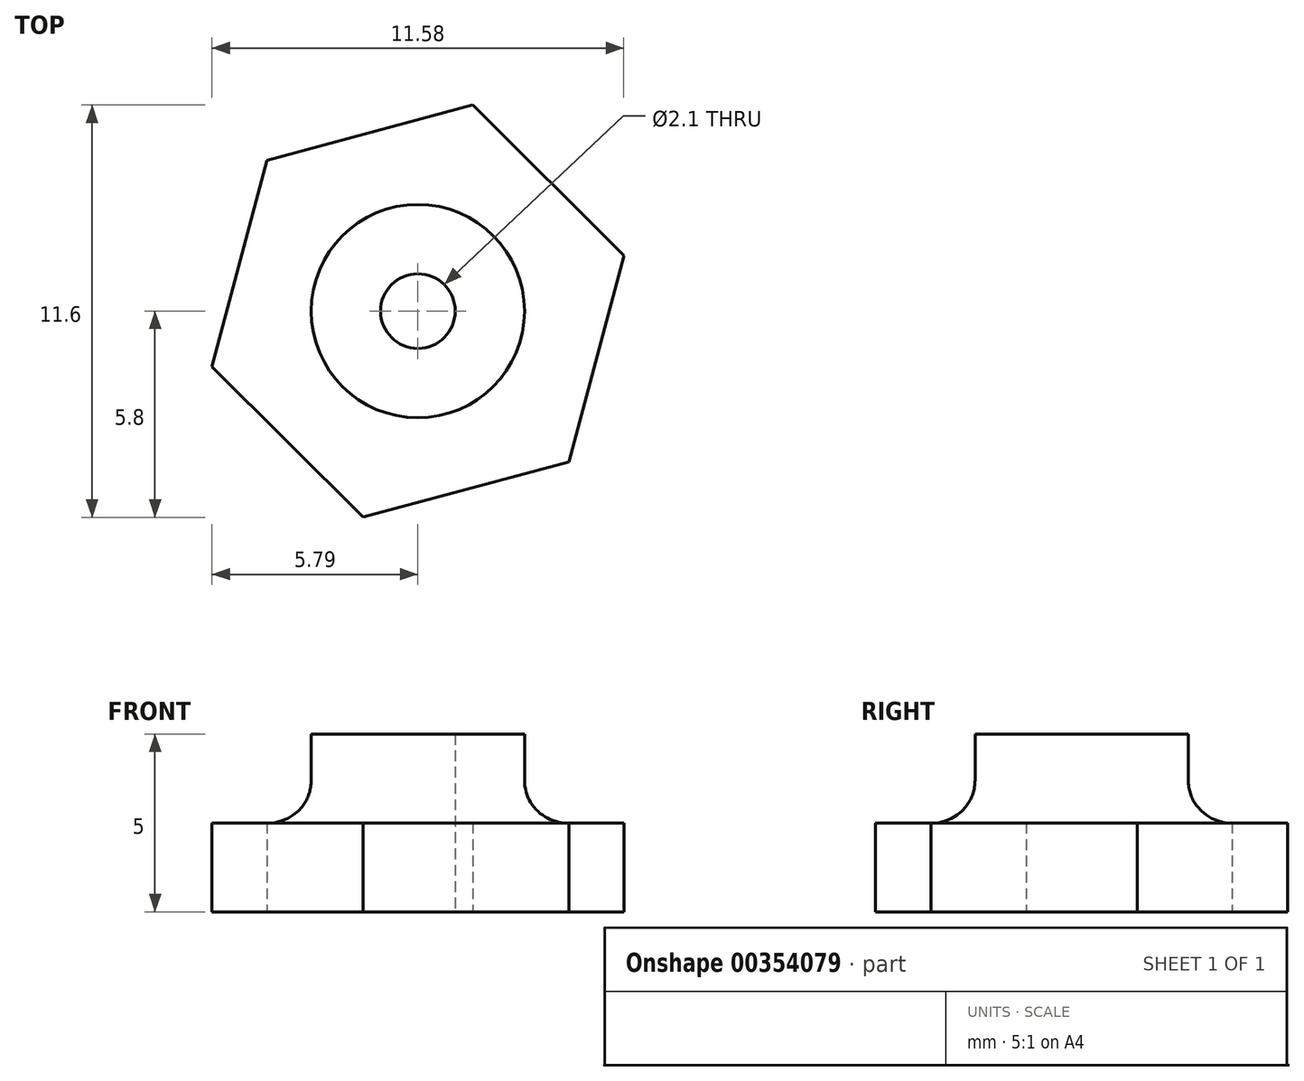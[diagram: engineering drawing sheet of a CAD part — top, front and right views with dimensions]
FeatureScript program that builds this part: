
annotation { "Feature Type Name" : "Feature", "Feature Type Description" : "" }
export const myFeature = defineFeature(function(context is Context, id is Id, definition is map)
    precondition{}
    {
        {
            var Q0;
            Q0=qCreatedBy(makeId("Top.planeOp"),FACE);
            var sketch = newSketch(context, id + "F0", { "sketchPlane" : qUnion([Q0])});
            skCircle(sketch, "E0", {"center": v(0, 0) * mm, "radius": 3 * mm});
            skCircle(sketch, "E1", {"center": v(0, 0) * mm, "radius": 1.05 * mm});
            skCircle(sketch, "E2.cCircle", {"center": v(0, 0) * mm, "radius": 6 * mm, "construction": true});
            skLineSegment(sketch, "E2.0", {"start": v(-4.25, 4.24) * mm, "end": v(1.55, 5.8) * mm});
            skLineSegment(sketch, "E2.1", {"start": v(1.55, 5.8) * mm, "end": v(5.8, 1.56) * mm});
            skLineSegment(sketch, "E2.2", {"start": v(5.8, 1.56) * mm, "end": v(4.25, -4.24) * mm});
            skLineSegment(sketch, "E2.3", {"start": v(4.25, -4.24) * mm, "end": v(-1.55, -5.8) * mm});
            skLineSegment(sketch, "E2.4", {"start": v(-1.55, -5.8) * mm, "end": v(-5.8, -1.56) * mm});
            skLineSegment(sketch, "E2.5", {"start": v(-5.8, -1.56) * mm, "end": v(-4.25, 4.24) * mm});
            skSolve(sketch);
        }
        {
            var Q0;
            Q0=makeQuery(id+"F0.imprint","IMPRINT",FACE,{"disambiguationData":[TD([[makeQuery(id+"F0.imprint","IMPRINT",EDGE,{"derivedFrom":sQuery(id+"F0.wireOp",EDGE,"E0")}),-1.0]])]});
            var Q1;
            Q1=makeQuery(id+"F0.imprint","IMPRINT",FACE,{"disambiguationData":[TD([[makeQuery(id+"F0.imprint","IMPRINT",EDGE,{"derivedFrom":sQuery(id+"F0.wireOp",EDGE,"E0")}),1.0]])]});
            extrude(context, id + "F1", {"entities" : qUnion([Q0, Q1]), "depth" : 2.5 * mm});
        }
        {
            var Q0;
            Q0=makeQuery(id+"F0.imprint","IMPRINT",FACE,{"disambiguationData":[TD([[makeQuery(id+"F0.imprint","IMPRINT",EDGE,{"derivedFrom":sQuery(id+"F0.wireOp",EDGE,"E0")}),1.0]])]});
            extrude(context, id + "F2", {"entities" : qUnion([Q0]), "operationType" : NewBodyOperationType.ADD, "depth" : 5 * mm});
        }
        {
            var Q0;
            Q0=makeQuery(id+"F2.boolean.opBoolean","INTERSECT",EDGE,{"derivedFrom":[makeQuery(id+"F1.opExtrude","CAP_FACE",FACE,{"disambiguationData":[OSD([sQuery(id+"F0.wireOp",EDGE,"E1"),sQuery(id+"F0.wireOp",EDGE,"E2.0"),sQuery(id+"F0.wireOp",EDGE,"E2.1"),sQuery(id+"F0.wireOp",EDGE,"E2.2"),sQuery(id+"F0.wireOp",EDGE,"E2.3"),sQuery(id+"F0.wireOp",EDGE,"E2.4"),sQuery(id+"F0.wireOp",EDGE,"E2.5")])],"isStart":false}),makeQuery(id+"F2.opExtrude","SWEPT_FACE",FACE,{"disambiguationData":[OSD([sQuery(id+"F0.wireOp",EDGE,"E0")])]})]});
            fillet(context, id + "F3", {"entities" : qUnion([Q0]), "radius" : 1.2 * mm, "tangentPropagation" : true, "allowEdgeOverflow" : false});
        }
    });
